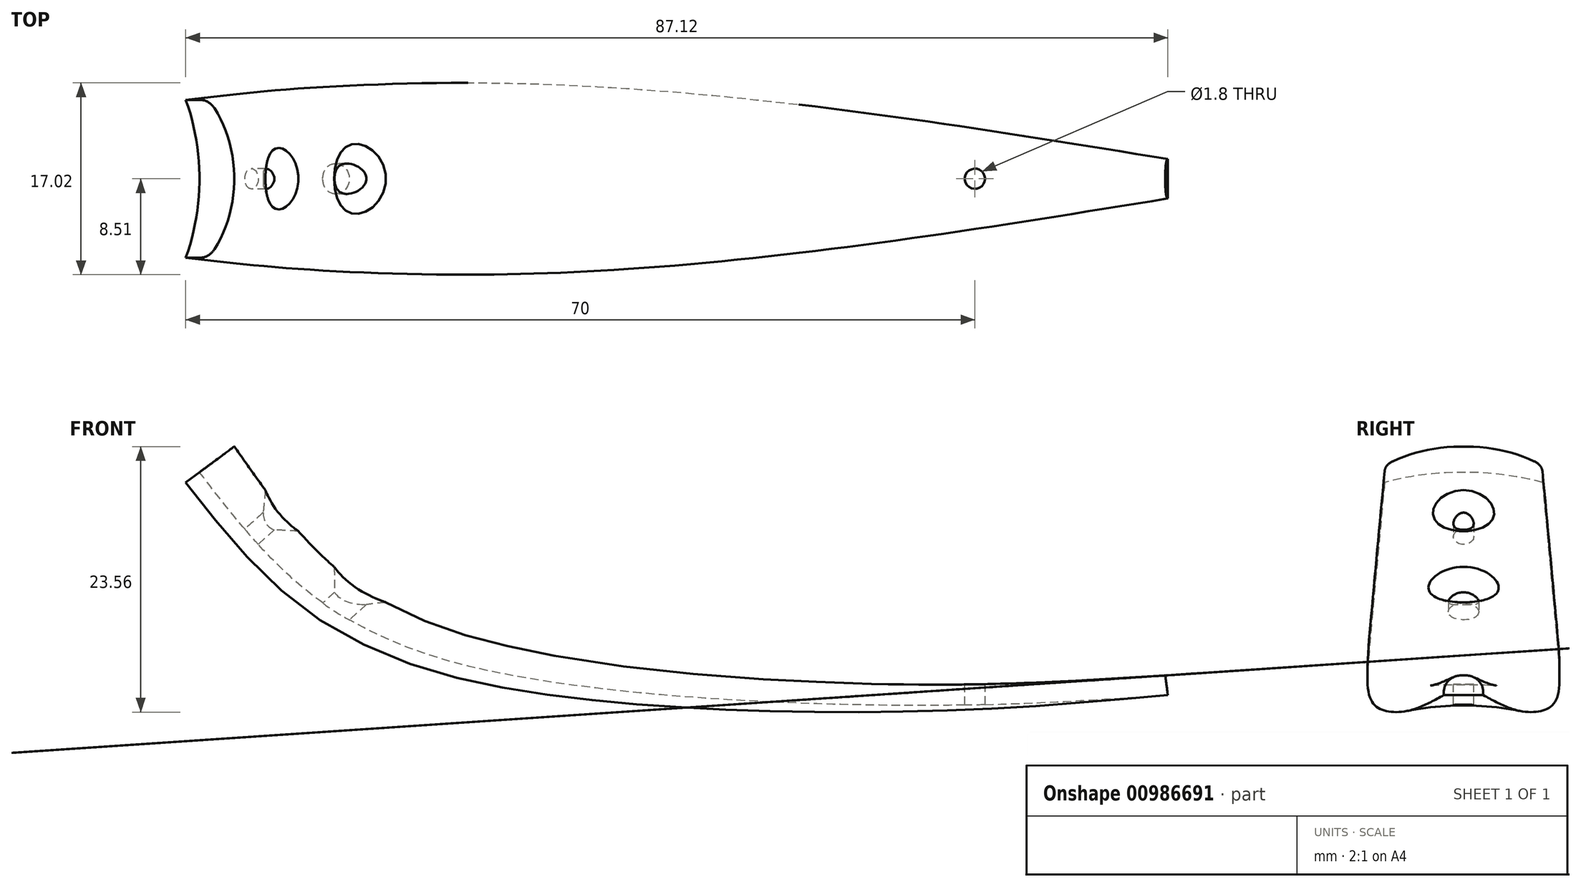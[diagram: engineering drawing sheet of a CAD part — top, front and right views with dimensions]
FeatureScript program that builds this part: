
annotation { "Feature Type Name" : "Feature", "Feature Type Description" : "" }
export const myFeature = defineFeature(function(context is Context, id is Id, definition is map)
    precondition{}
    {
        {
            var Q0;
            Q0=qCreatedBy(makeId("Front.planeOp"),FACE);
            var sketch = newSketch(context, id + "F0", { "sketchPlane" : qUnion([Q0])});
            skPoint(sketch, "E0", {"position": v(-27, 18) * mm});
            skPoint(sketch, "E1", {"position": v(60, 0) * mm});
            skFitSpline(sketch, "E2", {"points": [v(-27, 18) * mm, v(0, 0) * mm, v(60, 0) * mm], "startDerivative": vector(60.35, -81.72) * mm, "endDerivative": vector(94.02, 12.53) * mm});
            skPoint(sketch, "E3", {"position": v(-22.29, 12.17) * mm});
            skPoint(sketch, "E4", {"position": v(-14.8, 5.54) * mm});
            skPoint(sketch, "E5", {"position": v(43, -1.59) * mm});
            skSolve(sketch);
        }
        {
            var Q0;
            Q0=sQuery(id+"F0.wireOp",EDGE,"E2");
            var Q1;
            Q1=sQuery(id+"F0.wireOp",VERTEX,"E0");
            cPlane(context, id + "F1", {"entities" : qUnion([Q0, Q1]), "cplaneType" : CPlaneType.CURVE_POINT, "offset" : 25 * mm, "width" : 150 * mm, "height" : 150 * mm});
        }
        {
            var Q0;
            Q0=qCreatedBy(id+"F1.planeOp",FACE);
            var sketch = newSketch(context, id + "F2", { "sketchPlane" : qUnion([Q0])});
            skLineSegment(sketch, "E6", {"start": v(-11.03, 0) * mm, "end": v(-11.03, -7) * mm, "construction": true});
            skLineSegment(sketch, "E7", {"start": v(-11.03, 0) * mm, "end": v(-11.03, 7) * mm, "construction": true});
            skArc(sketch, "E8", {"start": v(-11.03, -7) * mm, "mid": v(-9.52, 0) * mm, "end": v(-11.03, 7) * mm});
            skLineSegment(sketch, "E9", {"start": v(-11.03, 7) * mm, "end": v(-9.42, 7) * mm});
            skLineSegment(sketch, "E10", {"start": v(-11.03, -7) * mm, "end": v(-9.42, -7) * mm});
            skArc(sketch, "E11", {"start": v(-7.86, -6.25) * mm, "mid": v(-5.67, 0) * mm, "end": v(-7.86, 6.25) * mm});
            skPoint(sketch, "E12.visualSharp", {"position": v(-8.53, 7) * mm});
            skArc(sketch, "E12.filletArc", {"start": v(-7.86, 6.25) * mm, "mid": v(-8.56, 6.8) * mm, "end": v(-9.42, 7) * mm});
            skPoint(sketch, "E13.visualSharp", {"position": v(-8.53, -7) * mm});
            skArc(sketch, "E13.filletArc", {"start": v(-9.42, -7) * mm, "mid": v(-8.56, -6.8) * mm, "end": v(-7.86, -6.25) * mm});
            skSolve(sketch);
        }
        {
            var Q0;
            Q0=sQuery(id+"F0.wireOp",EDGE,"E2");
            var Q1;
            Q1=sQuery(id+"F0.wireOp",VERTEX,"E2.1.internal");
            cPlane(context, id + "F3", {"entities" : qUnion([Q0, Q1]), "cplaneType" : CPlaneType.CURVE_POINT, "offset" : 25 * mm, "width" : 150 * mm, "height" : 150 * mm});
        }
        {
            var Q0;
            Q0=qCreatedBy(id+"F3.planeOp",FACE);
            var sketch = newSketch(context, id + "F4", { "sketchPlane" : qUnion([Q0])});
            skLineSegment(sketch, "E14", {"start": v(0, 0) * mm, "end": v(-8.5, 0) * mm, "construction": true});
            skLineSegment(sketch, "E15", {"start": v(0, 0) * mm, "end": v(0, -7.8) * mm, "construction": true});
            skLineSegment(sketch, "E16.MirrorCS", {"start": v(0, 0) * mm, "end": v(8.5, 0) * mm, "construction": true});
            skLineSegment(sketch, "E17", {"start": v(-8.5, 0) * mm, "end": v(-8.5, 0.96) * mm});
            skLineSegment(sketch, "E18.MirrorCS", {"start": v(8.5, 0) * mm, "end": v(8.5, 0.96) * mm});
            skArc(sketch, "E19", {"start": v(8.5, 0) * mm, "mid": v(0, 1.23) * mm, "end": v(-8.5, 0) * mm});
            skArc(sketch, "E20", {"start": v(6.96, 2.9) * mm, "mid": v(0, 3.73) * mm, "end": v(-6.96, 2.9) * mm});
            skPoint(sketch, "E21.visualSharp", {"position": v(-8.5, 2.5) * mm});
            skArc(sketch, "E21.filletArc", {"start": v(-6.96, 2.9) * mm, "mid": v(-8.07, 2.2) * mm, "end": v(-8.5, 0.96) * mm});
            skPoint(sketch, "E22.visualSharp", {"position": v(8.5, 2.5) * mm});
            skArc(sketch, "E22.filletArc", {"start": v(8.5, 0.96) * mm, "mid": v(8.07, 2.2) * mm, "end": v(6.96, 2.9) * mm});
            skSolve(sketch);
        }
        {
            var Q0;
            Q0=sQuery(id+"F0.wireOp",EDGE,"E2");
            var Q1;
            Q1=sQuery(id+"F0.wireOp",VERTEX,"E1");
            cPlane(context, id + "F5", {"entities" : qUnion([Q0, Q1]), "cplaneType" : CPlaneType.CURVE_POINT, "offset" : 25 * mm, "width" : 150 * mm, "height" : 150 * mm});
        }
        {
            var Q0;
            Q0=qCreatedBy(id+"F5.planeOp",FACE);
            var sketch = newSketch(context, id + "F6", { "sketchPlane" : qUnion([Q0])});
            skLineSegment(sketch, "E23.bottom", {"start": v(0.25, -7.05) * mm, "end": v(-0.25, -7.05) * mm});
            skLineSegment(sketch, "E23.top", {"start": v(1.75, -8.8) * mm, "end": v(-1.75, -8.8) * mm});
            skLineSegment(sketch, "E23.left", {"start": v(1.75, -8.55) * mm, "end": v(1.75, -8.8) * mm});
            skLineSegment(sketch, "E23.right", {"start": v(-1.75, -8.55) * mm, "end": v(-1.75, -8.8) * mm});
            skPoint(sketch, "E23.middle", {"position": v(0, -7.93) * mm});
            skPoint(sketch, "E24.visualSharp", {"position": v(1.75, -7.05) * mm});
            skArc(sketch, "E24.filletArc", {"start": v(1.75, -8.55) * mm, "mid": v(1.31, -7.5) * mm, "end": v(0.25, -7.05) * mm});
            skPoint(sketch, "E25.visualSharp", {"position": v(-1.75, -7.05) * mm});
            skArc(sketch, "E25.filletArc", {"start": v(-0.25, -7.05) * mm, "mid": v(-1.31, -7.5) * mm, "end": v(-1.75, -8.55) * mm});
            skSolve(sketch);
        }
        {
            var Q0;
            Q0=sQuery(id+"F0.wireOp",EDGE,"E2");
            var Q1;
            Q1 = qSketchRegion(id + "F2", true);
            var Q2;
            Q2 = qSketchRegion(id + "F4", true);
            var Q3;
            Q3 = qSketchRegion(id + "F6", true);
            loft(context, id + "F7", {"addSections" : true, "spine" : qUnion([Q0]), "sectionCount" : 5, "sheetProfilesArray" : [{ "sheetProfileEntities" : qUnion([Q1]) }, { "sheetProfileEntities" : qUnion([Q2]) }, { "sheetProfileEntities" : qUnion([Q3]) }]});
        }
        {
            var Q0;
            Q0=sQuery(id+"F0.wireOp",EDGE,"E2");
            var Q1;
            Q1=sQuery(id+"F0.wireOp",VERTEX,"E3");
            cPlane(context, id + "F8", {"entities" : qUnion([Q0, Q1]), "cplaneType" : CPlaneType.CURVE_POINT, "offset" : 25 * mm, "width" : 150 * mm, "height" : 150 * mm});
        }
        {
            var Q0;
            Q0=qCreatedBy(id+"F8.planeOp",FACE);
            var sketch = newSketch(context, id + "F9", { "sketchPlane" : qUnion([Q0])});
            skLineSegment(sketch, "E26", {"start": v(-8.42, 0) * mm, "end": v(10.87, 0) * mm, "construction": true});
            skLineSegment(sketch, "E27", {"start": v(10.87, 0) * mm, "end": v(-8.42, 0) * mm, "construction": true});
            skSolve(sketch);
        }
        {
            var Q0;
            Q0=sQuery(id+"F9.wireOp",EDGE,"E27");
            var Q1;
            Q1=sQuery(id+"F0.wireOp",VERTEX,"E3");
            cPlane(context, id + "F10", {"entities" : qUnion([Q0, Q1]), "cplaneType" : CPlaneType.CURVE_POINT, "offset" : 25 * mm, "width" : 150 * mm, "height" : 150 * mm});
        }
        {
            var Q0;
            Q0=qCreatedBy(id+"F10.planeOp",FACE);
            var sketch = newSketch(context, id + "F11", { "sketchPlane" : qUnion([Q0])});
            skCircle(sketch, "E28", {"center": v(0, 23.95) * mm, "radius": 0.9 * mm});
            skCircle(sketch, "E29", {"center": v(0, 14.02) * mm, "radius": 1.35 * mm});
            skSolve(sketch);
        }
        {
            var Q0;
            Q0 = qSketchRegion(id + "F11", true);
            extrude(context, id + "F12", {"entities" : qUnion([Q0]), "operationType" : NewBodyOperationType.REMOVE, "oppositeDirection" : true, "depth" : 25 * mm, "offsetDistance" : 25 * mm});
        }
        {
            var Q0;
            Q0=makeQuery(id+"F12.boolean.opBoolean","INTERSECT",EDGE,{"derivedFrom":[makeQuery(id+"F7.opLoft","SWEPT_FACE",FACE,{"disambiguationData":[OSD([sQuery(id+"F2.wireOp",EDGE,"E8"),sQuery(id+"F2.wireOp",EDGE,"E9"),sQuery(id+"F2.wireOp",EDGE,"E10"),sQuery(id+"F2.wireOp",EDGE,"E11"),sQuery(id+"F2.wireOp",EDGE,"E12.filletArc"),sQuery(id+"F2.wireOp",EDGE,"E13.filletArc"),sQuery(id+"F4.wireOp",EDGE,"E17"),sQuery(id+"F4.wireOp",EDGE,"E18.MirrorCS"),sQuery(id+"F4.wireOp",EDGE,"E19"),sQuery(id+"F4.wireOp",EDGE,"E20"),sQuery(id+"F4.wireOp",EDGE,"E21.filletArc"),sQuery(id+"F4.wireOp",EDGE,"E22.filletArc"),sQuery(id+"F6.wireOp",EDGE,"E23.bottom"),sQuery(id+"F6.wireOp",EDGE,"E23.top"),sQuery(id+"F6.wireOp",EDGE,"E23.left"),sQuery(id+"F6.wireOp",EDGE,"E23.right"),sQuery(id+"F6.wireOp",EDGE,"E24.filletArc"),sQuery(id+"F6.wireOp",EDGE,"E25.filletArc")])]}),makeQuery(id+"F12.opExtrude","SWEPT_FACE",FACE,{"disambiguationData":[OSD([sQuery(id+"F11.wireOp",EDGE,"E29")])]})]});
            var Q1;
            Q1=makeQuery(id+"F12.boolean.opBoolean","INTERSECT",EDGE,{"derivedFrom":[makeQuery(id+"F7.opLoft","SWEPT_FACE",FACE,{"disambiguationData":[OSD([sQuery(id+"F2.wireOp",EDGE,"E8"),sQuery(id+"F2.wireOp",EDGE,"E9"),sQuery(id+"F2.wireOp",EDGE,"E10"),sQuery(id+"F2.wireOp",EDGE,"E11"),sQuery(id+"F2.wireOp",EDGE,"E12.filletArc"),sQuery(id+"F2.wireOp",EDGE,"E13.filletArc"),sQuery(id+"F4.wireOp",EDGE,"E17"),sQuery(id+"F4.wireOp",EDGE,"E18.MirrorCS"),sQuery(id+"F4.wireOp",EDGE,"E19"),sQuery(id+"F4.wireOp",EDGE,"E20"),sQuery(id+"F4.wireOp",EDGE,"E21.filletArc"),sQuery(id+"F4.wireOp",EDGE,"E22.filletArc"),sQuery(id+"F6.wireOp",EDGE,"E23.bottom"),sQuery(id+"F6.wireOp",EDGE,"E23.top"),sQuery(id+"F6.wireOp",EDGE,"E23.left"),sQuery(id+"F6.wireOp",EDGE,"E23.right"),sQuery(id+"F6.wireOp",EDGE,"E24.filletArc"),sQuery(id+"F6.wireOp",EDGE,"E25.filletArc")])]}),makeQuery(id+"F12.opExtrude","SWEPT_FACE",FACE,{"disambiguationData":[OSD([sQuery(id+"F11.wireOp",EDGE,"E28")])]})]});
            chamfer(context, id + "F13", {"entities" : qUnion([Q0, Q1]), "width" : 1.5 * mm, "tangentPropagation" : true});
        }
        {
            var Q0;
            Q0=qCreatedBy(makeId("Top.planeOp"),FACE);
            var sketch = newSketch(context, id + "F14", { "sketchPlane" : qUnion([Q0])});
            skCircle(sketch, "E30", {"center": v(43, 0) * mm, "radius": 0.9 * mm});
            skSolve(sketch);
        }
        {
            var Q0;
            Q0 = qSketchRegion(id + "F14", true);
            extrude(context, id + "F15", {"entities" : qUnion([Q0]), "operationType" : NewBodyOperationType.REMOVE, "oppositeDirection" : true, "depth" : 25 * mm, "offsetDistance" : 25 * mm, "hasSecondDirection" : true, "secondDirectionOppositeDirection" : false, "secondDirectionDepth" : 25 * mm});
        }
    });
